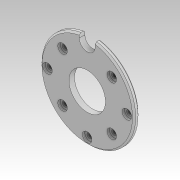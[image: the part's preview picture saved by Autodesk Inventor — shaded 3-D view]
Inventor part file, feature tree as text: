
AUTODESK INVENTOR PART (.ipt)
format: ipt  version: 2020 (Build 240168000, 168)  size: 177,664 bytes
history: native  units: mm
features: extrude x3, sketch x3, chamfer x1
ambient origin geometry x8: Origin, YZ Plane, XZ Plane, XY Plane, X Axis, Y Axis, Z Axis, Center Point
bodies: Solid1 (feature_tree)
feature tree (7):
  extrude  "Extrusion1"  Depth=3.3mm
  extrude  "Extrusion2"  Depth=31.0mm
  extrude  "Extrusion3"  Depth=3.0mm
  chamfer  "Chamfer1"  Distance=3.5mm
  sketch  "Sketch1"  dims[d0=59.0mm d1=3.3mm]
  sketch  "Sketch2"  dims[d2=23.0mm d3=31.0mm]
  sketch  "Sketch3"  dims[d4=50.0mm d5=3.3mm d6=3.5mm d7=0.0mm d8=6.0mm d9=1.5mm d10=0.0mm d11=1.0mm d12=2.0mm d13=45.0deg d14=3.0mm d15=5.0mm d16=0.0mm d17=0.0mm]
